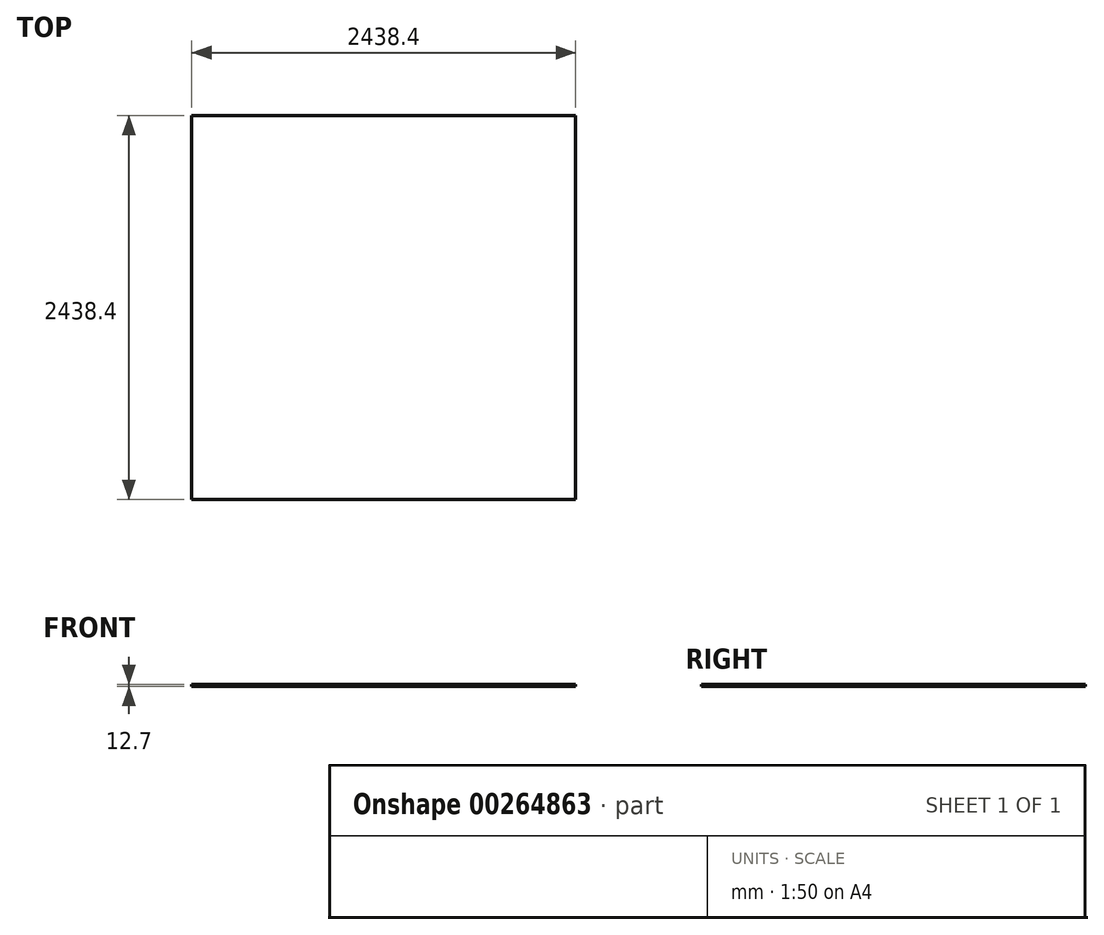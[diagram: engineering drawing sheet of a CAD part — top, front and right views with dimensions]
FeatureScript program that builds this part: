
annotation { "Feature Type Name" : "Feature", "Feature Type Description" : "" }
export const myFeature = defineFeature(function(context is Context, id is Id, definition is map)
    precondition{}
    {
        {
            var Q0;
            Q0=qCreatedBy(makeId("Top.planeOp"),FACE);
            var sketch = newSketch(context, id + "F0", { "sketchPlane" : qUnion([Q0])});
            skLineSegment(sketch, "E0.bottom", {"start": v(0, 0) * mm, "end": v(2438.4, 0) * mm});
            skLineSegment(sketch, "E0.top", {"start": v(0, 2438.4) * mm, "end": v(2438.4, 2438.4) * mm});
            skLineSegment(sketch, "E0.left", {"start": v(0, 0) * mm, "end": v(0, 2438.4) * mm});
            skLineSegment(sketch, "E0.right", {"start": v(2438.4, 0) * mm, "end": v(2438.4, 2438.4) * mm});
            skSolve(sketch);
        }
        {
            var Q0;
            Q0=makeQuery(id+"F0.imprint","IMPRINT",FACE,{"disambiguationData":[TD([[makeQuery(id+"F0.imprint","IMPRINT",EDGE,{"derivedFrom":sQuery(id+"F0.wireOp",EDGE,"E0.bottom")}),1.0]])]});
            extrude(context, id + "F1", {"entities" : qUnion([Q0]), "depth" : 12.7 * mm});
        }
    });
